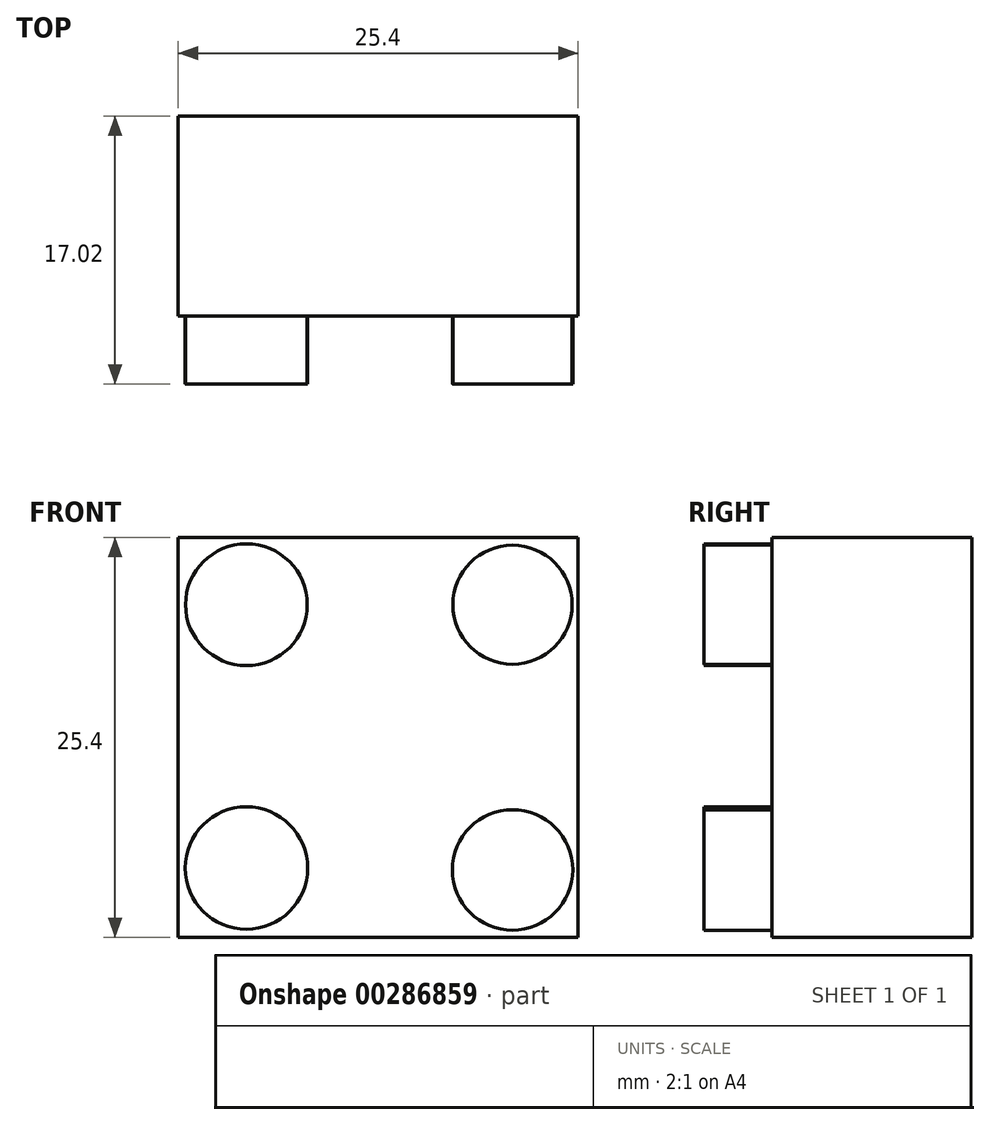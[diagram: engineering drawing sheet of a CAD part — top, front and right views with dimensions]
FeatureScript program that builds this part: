
annotation { "Feature Type Name" : "Feature", "Feature Type Description" : "" }
export const myFeature = defineFeature(function(context is Context, id is Id, definition is map)
    precondition{}
    {
        {
            var Q0;
            Q0=qCreatedBy(makeId("Front.planeOp"),FACE);
            var sketch = newSketch(context, id + "F0", { "sketchPlane" : qUnion([Q0])});
            skLineSegment(sketch, "E0", {"start": v(-12.64, 8.95) * mm, "end": v(-12.64, -16.45) * mm});
            skLineSegment(sketch, "E1", {"start": v(12.76, -16.45) * mm, "end": v(12.76, 8.95) * mm});
            skLineSegment(sketch, "E2", {"start": v(12.76, 8.95) * mm, "end": v(-12.64, 8.95) * mm});
            skLineSegment(sketch, "E3", {"start": v(-12.64, -16.45) * mm, "end": v(12.76, -16.45) * mm});
            skSolve(sketch);
        }
        {
            var Q0;
            Q0=makeQuery(id+"F0.imprint","IMPRINT",FACE,{"disambiguationData":[TD([[makeQuery(id+"F0.imprint","IMPRINT",EDGE,{"derivedFrom":sQuery(id+"F0.wireOp",EDGE,"E0")}),1.0]])]});
            extrude(context, id + "F1", {"entities" : qUnion([Q0]), "depth" : 12.7 * mm});
        }
        {
            var Q0;
            Q0=qCreatedBy(makeId("Front.planeOp"),FACE);
            var sketch = newSketch(context, id + "F2", { "sketchPlane" : qUnion([Q0])});
            skCircle(sketch, "E4", {"center": v(8.6, 4.68) * mm, "radius": 3.79 * mm});
            skCircle(sketch, "E5", {"center": v(-8.3, -12.05) * mm, "radius": 3.9 * mm});
            skCircle(sketch, "E6", {"center": v(-8.3, 4.68) * mm, "radius": 3.86 * mm});
            skCircle(sketch, "E7", {"center": v(8.6, -12.16) * mm, "radius": 3.83 * mm});
            skSolve(sketch);
        }
        {
            var Q0;
            Q0=makeQuery(id+"F2.imprint","IMPRINT",FACE,{"disambiguationData":[TD([[makeQuery(id+"F2.imprint","IMPRINT",EDGE,{"derivedFrom":sQuery(id+"F2.wireOp",EDGE,"E5")}),1.0]])]});
            extrude(context, id + "F3", {"entities" : qUnion([Q0]), "operationType" : NewBodyOperationType.ADD, "depth" : 17.02 * mm});
        }
        {
            var Q0;
            Q0=makeQuery(id+"F2.imprint","IMPRINT",FACE,{"disambiguationData":[TD([[makeQuery(id+"F2.imprint","IMPRINT",EDGE,{"derivedFrom":sQuery(id+"F2.wireOp",EDGE,"E7")}),1.0]])]});
            extrude(context, id + "F4", {"entities" : qUnion([Q0]), "operationType" : NewBodyOperationType.ADD, "depth" : 17.02 * mm});
        }
        {
            var Q0;
            Q0=makeQuery(id+"F2.imprint","IMPRINT",FACE,{"disambiguationData":[TD([[makeQuery(id+"F2.imprint","IMPRINT",EDGE,{"derivedFrom":sQuery(id+"F2.wireOp",EDGE,"E6")}),1.0]])]});
            extrude(context, id + "F5", {"entities" : qUnion([Q0]), "operationType" : NewBodyOperationType.ADD, "depth" : 17.02 * mm});
        }
        {
            var Q0;
            Q0=makeQuery(id+"F2.imprint","IMPRINT",FACE,{"disambiguationData":[TD([[makeQuery(id+"F2.imprint","IMPRINT",EDGE,{"derivedFrom":sQuery(id+"F2.wireOp",EDGE,"E4")}),1.0]])]});
            extrude(context, id + "F6", {"entities" : qUnion([Q0]), "operationType" : NewBodyOperationType.ADD, "depth" : 17.02 * mm});
        }
    });
